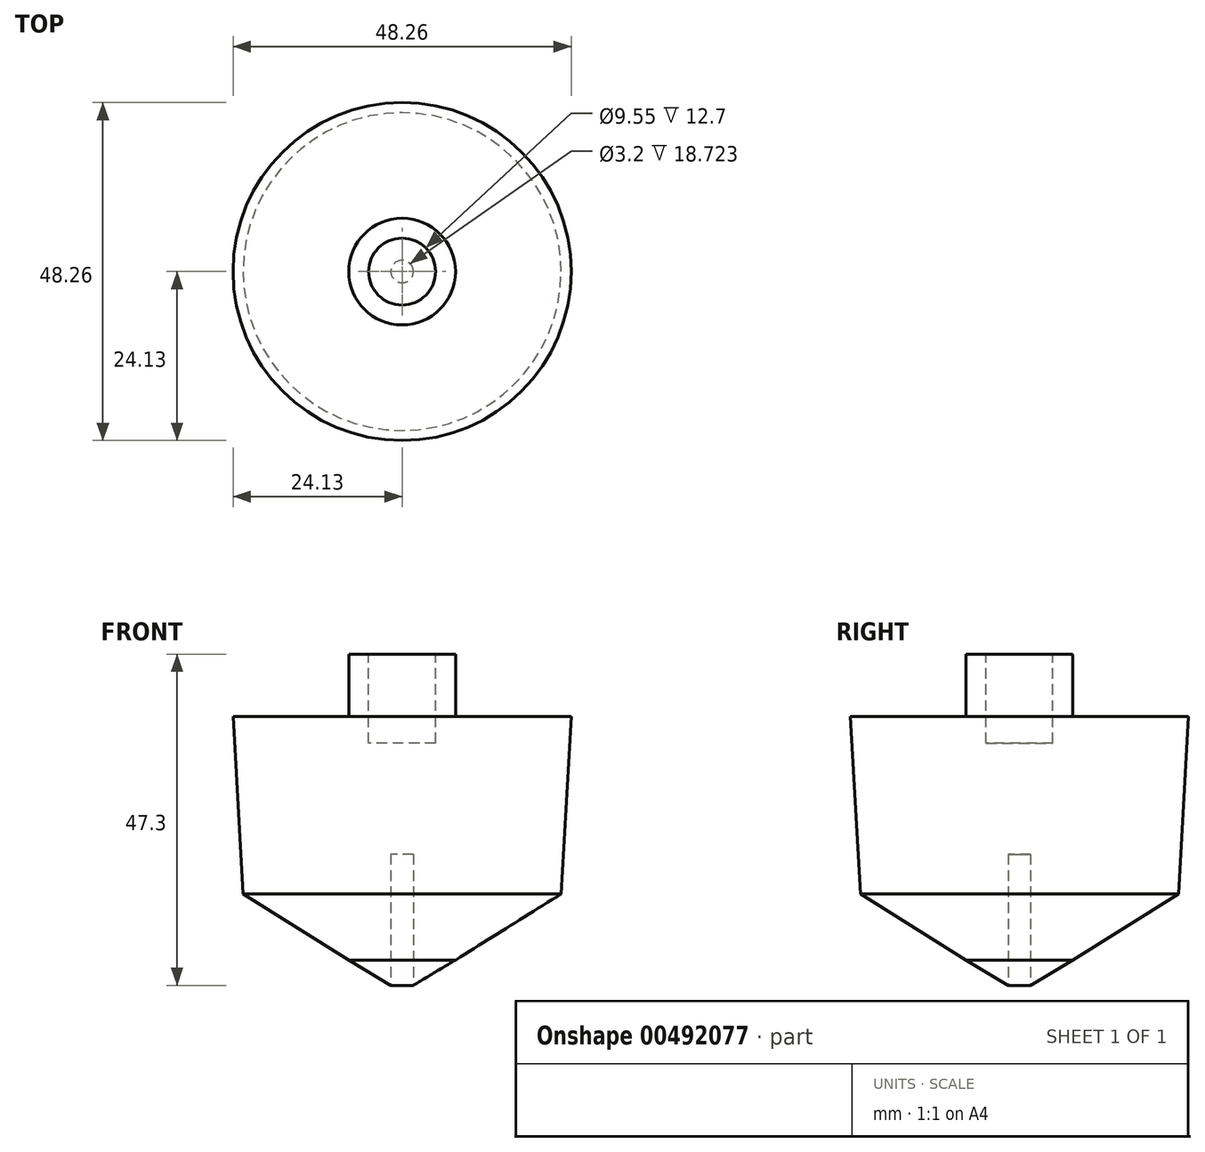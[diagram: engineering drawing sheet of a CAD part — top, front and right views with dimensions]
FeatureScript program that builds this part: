
annotation { "Feature Type Name" : "Feature", "Feature Type Description" : "" }
export const myFeature = defineFeature(function(context is Context, id is Id, definition is map)
    precondition{}
    {
        {
            var Q0;
            Q0=qCreatedBy(makeId("Front.planeOp"),FACE);
            var sketch = newSketch(context, id + "F0", { "sketchPlane" : qUnion([Q0])});
            skLineSegment(sketch, "E0", {"start": v(0, 0) * mm, "end": v(7.62, 4.58) * mm});
            skLineSegment(sketch, "E1", {"start": v(7.62, 4.58) * mm, "end": v(22.7, 14.01) * mm});
            skLineSegment(sketch, "E2", {"start": v(22.7, 14.01) * mm, "end": v(24.13, 39.37) * mm});
            skLineSegment(sketch, "E3", {"start": v(24.13, 39.37) * mm, "end": v(7.62, 39.37) * mm});
            skLineSegment(sketch, "E4", {"start": v(7.62, 39.37) * mm, "end": v(7.62, 48.26) * mm});
            skLineSegment(sketch, "E5", {"start": v(7.62, 48.26) * mm, "end": v(0, 48.26) * mm});
            skLineSegment(sketch, "E6", {"start": v(0, 48.26) * mm, "end": v(0, 0) * mm});
            skSolve(sketch);
        }
        {
            var Q0;
            Q0=makeQuery(id+"F0.imprint","IMPRINT",FACE,{"disambiguationData":[TD([[makeQuery(id+"F0.imprint","IMPRINT",EDGE,{"derivedFrom":sQuery(id+"F0.wireOp",EDGE,"E0")}),1.0]])]});
            var Q1;
            Q1=sQuery(id+"F0.wireOp",EDGE,"E6");
            revolve(context, id + "F1", {"entities" : qUnion([Q0]), "axis" : qUnion([Q1]), "revolveType" : RevolveType.FULL});
        }
        {
            var Q0;
            Q0=makeQuery(id+"F1.opRevolve","SWEPT_FACE",FACE,{"disambiguationData":[OSD([sQuery(id+"F0.wireOp",EDGE,"E5")])]});
            var sketch = newSketch(context, id + "F2", { "sketchPlane" : qUnion([Q0])});
            skCircle(sketch, "E7", {"center": v(0, 0) * mm, "radius": 4.78 * mm});
            skSolve(sketch);
        }
        {
            var Q0;
            Q0=makeQuery(id+"F2.imprint","IMPRINT",FACE,{"disambiguationData":[TD([[makeQuery(id+"F2.imprint","IMPRINT",EDGE,{"derivedFrom":sQuery(id+"F2.wireOp",EDGE,"E7")}),1.0]])]});
            var Q1;
            Q1=sQuery(id+"F2.wireOp",EDGE,"E7");
            extrude(context, id + "F3", {"entities" : qUnion([Q0]), "operationType" : NewBodyOperationType.REMOVE, "surfaceEntities" : qUnion([Q1]), "oppositeDirection" : true, "depth" : 12.7 * mm});
        }
        {
            var Q0;
            Q0=qCreatedBy(makeId("Top.planeOp"),FACE);
            var sketch = newSketch(context, id + "F4", { "sketchPlane" : qUnion([Q0])});
            skCircle(sketch, "E8", {"center": v(0, 0) * mm, "radius": 1.6 * mm});
            skSolve(sketch);
        }
        {
            var Q0;
            Q0=makeQuery(id+"F4.imprint","IMPRINT",FACE,{"disambiguationData":[TD([[makeQuery(id+"F4.imprint","IMPRINT",EDGE,{"derivedFrom":sQuery(id+"F4.wireOp",EDGE,"E8")}),1.0]])]});
            var Q1;
            Q1=sQuery(id+"F4.wireOp",EDGE,"E8");
            extrude(context, id + "F5", {"entities" : qUnion([Q0]), "operationType" : NewBodyOperationType.REMOVE, "surfaceEntities" : qUnion([Q1]), "depth" : 19.68 * mm});
        }
    });
